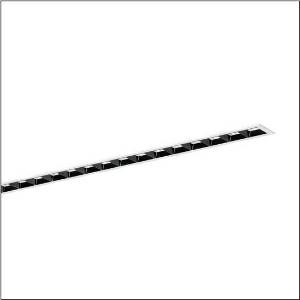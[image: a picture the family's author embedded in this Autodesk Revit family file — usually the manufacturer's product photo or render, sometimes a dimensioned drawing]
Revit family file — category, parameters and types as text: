
# Revit family: silica_21_51mx11tbt5w
name_source: partatom
category: Lighting Fixtures
units: mm (PartAtom-declared; Revit-internal decimal feet)

## family parameters
Cut with Voids When Loaded = No
Host = Face
Light Source = No
Part Type = Normal
Room Calculation Point = No
Round Connector Dimension = Use Diameter
Shared = No

## types (1)
- --- (1 x LED, 4650 lm, 40.3 W, 6500K)
    Apparent Load = 40 VA
    CIE Flux Codes = 85 99 100 100 100
    Color Rendering = 80
    Color Temperature = 6500K
    Default Elevation = 1800 mm
    Description = Silica 21, office luminaire, primary light control with darklight reflector, of PMMA, black, CAT 2 (L<= 3000cd/m²), light emission: direct distribution, primary light characteristic: symmetric, installation type: recessed, LED, rated luminous flux: 4.650lm, luminous efficacy: 110lm/W, light colour: 8tw, colour temperature: 2700..6500K, control gear: DALI DT8, with terminal, 3+2-pole, max. 2.5mm², mains connection: 220..240V, AC, 50/60Hz, rated input power: 42.3W, luminaire housing, of aluminium, traffic white (RAL 9016), length: 1.528mm, width: 79mm, height: 53mm, protection rating (complete): IP20, insulation class (complete): insulation class I (protective earthing), certification: CE, ENEC, VDE, permissible operating ambient temperature: 0..+35°C, standard: EN 50419, packaging unit: 1 piece
    Height = 0 mm  [stored 0 ft]
    Lamp = 1 x LED
    Lamp Light Flux = 4650 lm
    Lamp Power = 40.3 W
    Lamp count = 1
    Length = 1527 mm
    Luminous efficacy = 115 lm/W
    Manufacturer = Siteco
    ModVariant = No
    Model = 51MX11TBT5W
    Mounting Place = Ceiling
    Mounting Type = Recessed
    Number of Poles = 1
    OnlyDefault = Yes
    Power Factor = 1
    Product Name = Silica 21
    Product group = office luminaire | ceiling recessed
    ProductGroupID = 400
    Protection Class = Protection class I
    Protection Degree = IP 20
    RLX_Detail_Level = 1
    RLX_Emergency_Light_Flux = 0 lm
    RLX_Emergency_Type = 0
    RLX_Emergency_Type_DB = No
    RlxData = <blob elided: 39113 chars, md5=6b1e6db1>
    Socket = socket
    Standby Power = 0 W
    System Light Flux = 4650 lm
    System Power = 40 W
    Type Comments = individual setting
    Type Image = l_1335880.jpg
    URL = http://relux.com
    VarID = @adj_139595
    Voltage = 0 V
    Weight = 0.00 kg
    Width = 79 mm

note: [stored X ft] marks values corroborated as IEEE doubles in the binary element streams (Revit-internal decimal feet)

## geometry (parser evidence)
native form markers: Blend x4, Sweep x11
no freeform markers — native parametric forms only
